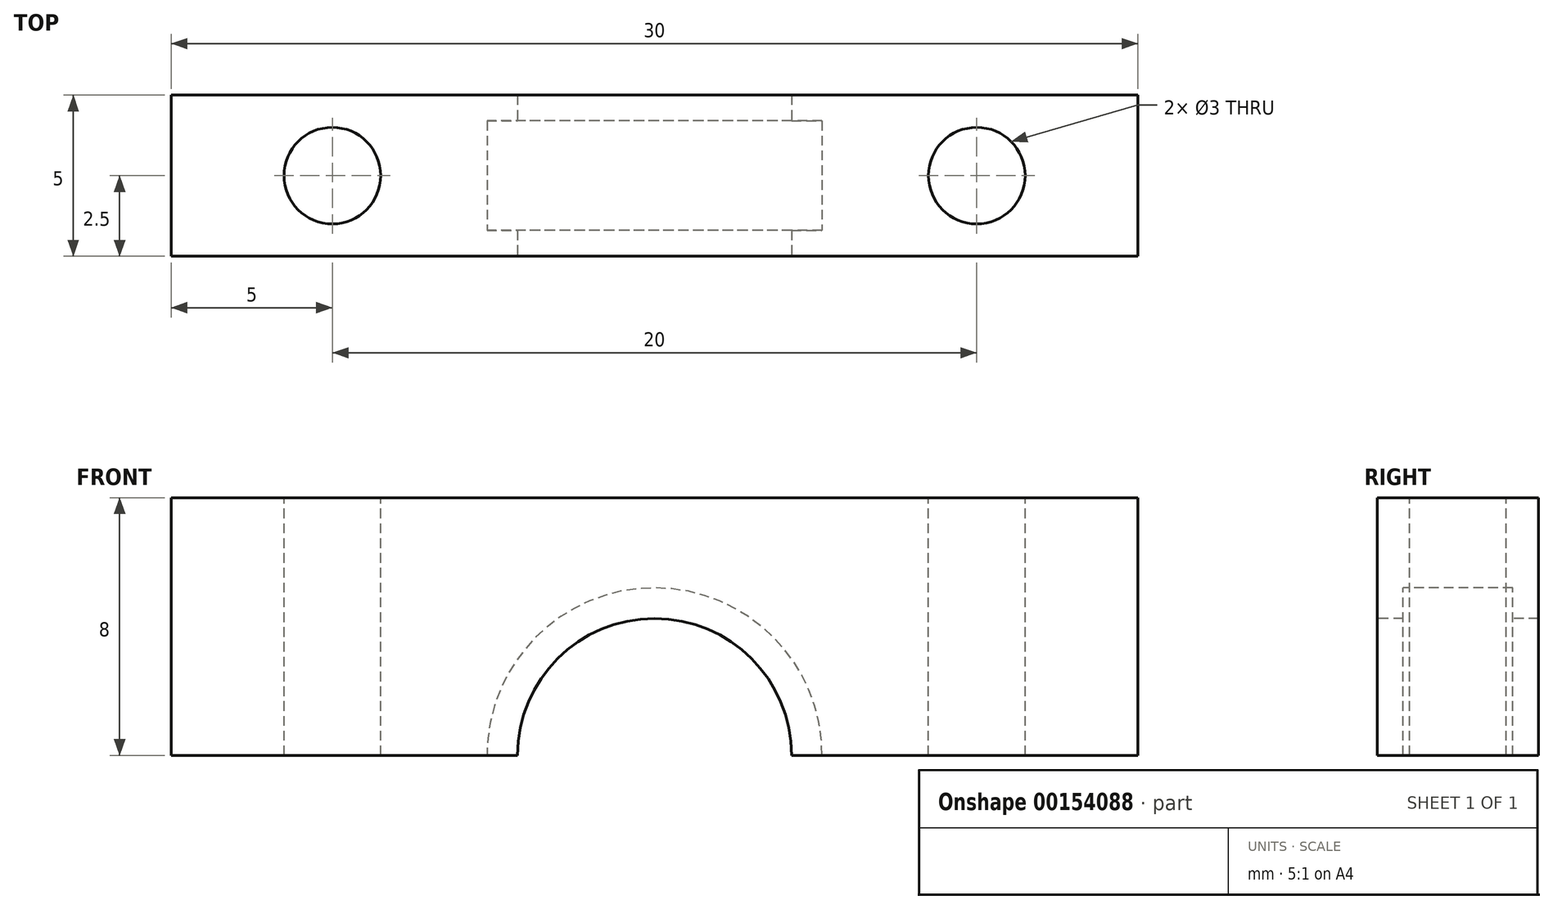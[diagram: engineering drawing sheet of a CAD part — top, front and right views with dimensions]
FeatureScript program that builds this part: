
annotation { "Feature Type Name" : "Feature", "Feature Type Description" : "" }
export const myFeature = defineFeature(function(context is Context, id is Id, definition is map)
    precondition{}
    {
        {
            var Q0;
            Q0=qCreatedBy(makeId("Top.planeOp"),FACE);
            var sketch = newSketch(context, id + "F0", { "sketchPlane" : qUnion([Q0])});
            skLineSegment(sketch, "E0.bottom", {"start": v(-15, 2.5) * mm, "end": v(15, 2.5) * mm});
            skLineSegment(sketch, "E0.top", {"start": v(-15, -2.5) * mm, "end": v(15, -2.5) * mm});
            skLineSegment(sketch, "E0.left", {"start": v(-15, 2.5) * mm, "end": v(-15, -2.5) * mm});
            skLineSegment(sketch, "E0.right", {"start": v(15, 2.5) * mm, "end": v(15, -2.5) * mm});
            skSolve(sketch);
        }
        {
            var Q0;
            Q0 = qSketchRegion(id + "F0", true);
            extrude(context, id + "F1", {"entities" : qUnion([Q0]), "depth" : 8 * mm});
        }
        {
            var Q0;
            Q0=qCreatedBy(makeId("Front.planeOp"),FACE);
            var sketch = newSketch(context, id + "F2", { "sketchPlane" : qUnion([Q0])});
            skCircle(sketch, "E1", {"center": v(0, 0) * mm, "radius": 4.25 * mm});
            skSolve(sketch);
        }
        {
            var Q0;
            Q0 = qSketchRegion(id + "F2", true);
            extrude(context, id + "F3", {"entities" : qUnion([Q0]), "operationType" : NewBodyOperationType.REMOVE, "oppositeDirection" : true, "depth" : 10 * mm, "symmetric" : true});
        }
        {
            var Q0;
            Q0=qCreatedBy(makeId("Front.planeOp"),FACE);
            var sketch = newSketch(context, id + "F4", { "sketchPlane" : qUnion([Q0])});
            skCircle(sketch, "E2", {"center": v(0, 0) * mm, "radius": 5.2 * mm});
            skSolve(sketch);
        }
        {
            var Q0;
            Q0 = qSketchRegion(id + "F4", true);
            extrude(context, id + "F5", {"entities" : qUnion([Q0]), "operationType" : NewBodyOperationType.REMOVE, "oppositeDirection" : true, "depth" : 3.4 * mm, "symmetric" : true});
        }
        {
            var Q0;
            Q0=makeQuery(id+"F1.opExtrude","CAP_FACE",FACE,{"disambiguationData":[OSD([sQuery(id+"F0.wireOp",EDGE,"E0.bottom"),sQuery(id+"F0.wireOp",EDGE,"E0.top"),sQuery(id+"F0.wireOp",EDGE,"E0.left"),sQuery(id+"F0.wireOp",EDGE,"E0.right")])],"isStart":false});
            var sketch = newSketch(context, id + "F6", { "sketchPlane" : qUnion([Q0])});
            skCircle(sketch, "E3", {"center": v(-10, 0) * mm, "radius": 1.5 * mm});
            skCircle(sketch, "E4", {"center": v(10, 0) * mm, "radius": 1.5 * mm});
            skSolve(sketch);
        }
        {
            var Q0;
            Q0 = qSketchRegion(id + "F6", true);
            extrude(context, id + "F7", {"entities" : qUnion([Q0]), "operationType" : NewBodyOperationType.REMOVE, "endBound" : BoundingType.THROUGH_ALL, "oppositeDirection" : true, "depth" : 25 * mm});
        }
    });
